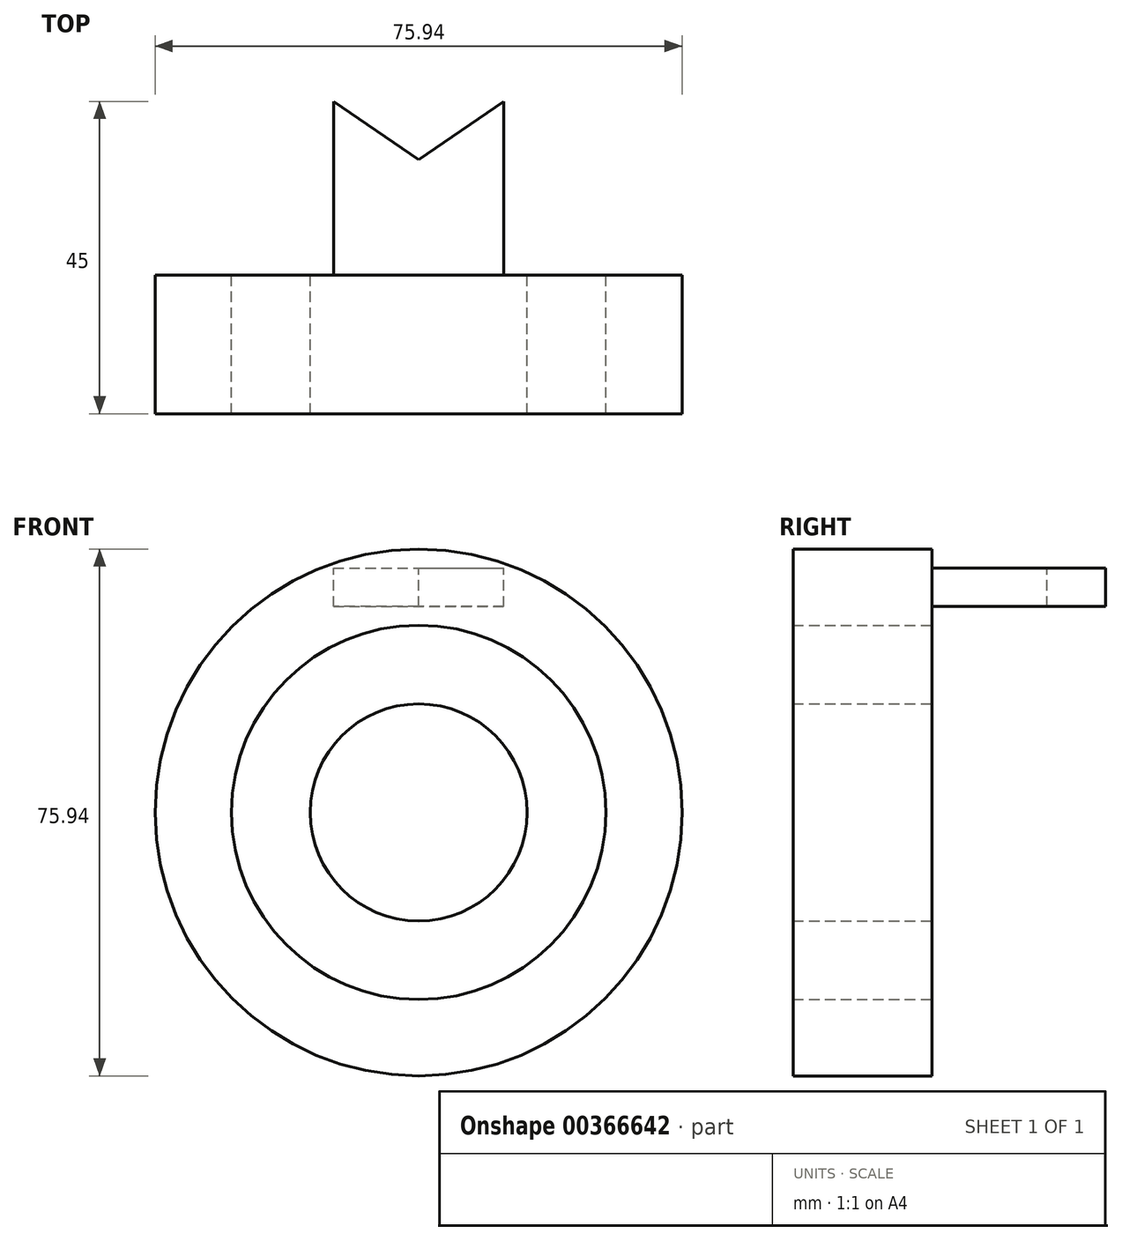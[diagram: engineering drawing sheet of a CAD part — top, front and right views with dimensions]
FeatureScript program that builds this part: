
annotation { "Feature Type Name" : "Feature", "Feature Type Description" : "" }
export const myFeature = defineFeature(function(context is Context, id is Id, definition is map)
    precondition{}
    {
        {
            var Q0;
            Q0=qCreatedBy(makeId("Front.planeOp"),FACE);
            var sketch = newSketch(context, id + "F0", { "sketchPlane" : qUnion([Q0])});
            skCircle(sketch, "E0", {"center": v(0, 0) * mm, "radius": 37.97 * mm});
            skCircle(sketch, "E1", {"center": v(0, 0) * mm, "radius": 26.98 * mm});
            skCircle(sketch, "E2", {"center": v(0, 0) * mm, "radius": 15.64 * mm});
            skSolve(sketch);
        }
        {
            var Q0;
            Q0=makeQuery(id+"F0.imprint","IMPRINT",FACE,{"disambiguationData":[TD([[makeQuery(id+"F0.imprint","IMPRINT",EDGE,{"derivedFrom":sQuery(id+"F0.wireOp",EDGE,"E0")}),1.0]])]});
            var Q1;
            Q1=makeQuery(id+"F0.imprint","IMPRINT",FACE,{"disambiguationData":[TD([[makeQuery(id+"F0.imprint","IMPRINT",EDGE,{"derivedFrom":sQuery(id+"F0.wireOp",EDGE,"E2")}),1.0]])]});
            extrude(context, id + "F1", {"entities" : qUnion([Q0, Q1]), "depth" : 10 * mm, "hasSecondDirection" : true, "secondDirectionOppositeDirection" : true, "secondDirectionDepth" : 10 * mm});
        }
        {
            var Q0;
            Q0=makeQuery(id+"F1.opExtrude","CAP_FACE",FACE,{"disambiguationData":[OSD([sQuery(id+"F0.wireOp",EDGE,"E0"),sQuery(id+"F0.wireOp",EDGE,"E1")])],"isStart":true});
            var sketch = newSketch(context, id + "F2", { "sketchPlane" : qUnion([Q0])});
            skLineSegment(sketch, "E3.bottom", {"start": v(12.27, 29.68) * mm, "end": v(-12.27, 29.68) * mm});
            skLineSegment(sketch, "E3.top", {"start": v(12.27, 35.21) * mm, "end": v(-12.27, 35.21) * mm});
            skLineSegment(sketch, "E3.left", {"start": v(12.27, 29.68) * mm, "end": v(12.27, 35.21) * mm});
            skLineSegment(sketch, "E3.right", {"start": v(-12.27, 29.68) * mm, "end": v(-12.27, 35.21) * mm});
            skPoint(sketch, "E3.middle", {"position": v(0, 32.45) * mm});
            skSolve(sketch);
        }
        {
            var Q0;
            Q0=makeQuery(id+"F2.imprint","IMPRINT",FACE,{"disambiguationData":[TD([[makeQuery(id+"F2.imprint","IMPRINT",EDGE,{"derivedFrom":sQuery(id+"F2.wireOp",EDGE,"E3.bottom")}),-1.0]])]});
            extrude(context, id + "F3", {"entities" : qUnion([Q0]), "operationType" : NewBodyOperationType.ADD, "depth" : 25 * mm});
        }
        {
            var Q0;
            Q0=makeQuery(id+"F3.opExtrude","SWEPT_FACE",FACE,{"disambiguationData":[OSD([sQuery(id+"F2.wireOp",EDGE,"E3.top")])]});
            var sketch = newSketch(context, id + "F4", { "sketchPlane" : qUnion([Q0])});
            skLineSegment(sketch, "E4", {"start": v(-12.27, 35) * mm, "end": v(0, 26.6) * mm});
            skLineSegment(sketch, "E5", {"start": v(0, 26.6) * mm, "end": v(12.27, 35) * mm});
            skSolve(sketch);
        }
        {
            var Q0;
            Q0=makeQuery(id+"F4.imprint","IMPRINT",FACE,{"disambiguationData":[TD([[makeQuery(id+"F4.imprint","IMPRINT",EDGE,{"derivedFrom":sQuery(id+"F4.wireOp",EDGE,"E4")}),1.0]])]});
            extrude(context, id + "F5", {"entities" : qUnion([Q0]), "operationType" : NewBodyOperationType.REMOVE, "oppositeDirection" : true, "depth" : 25 * mm});
        }
    });
